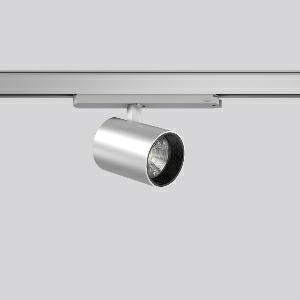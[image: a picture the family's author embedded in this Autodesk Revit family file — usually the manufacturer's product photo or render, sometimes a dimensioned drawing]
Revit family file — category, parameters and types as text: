
# Revit family: deecos_s_mini_track-in_742264_004_3_135f
name_source: partatom
category: Lighting Fixtures
units: mm (PartAtom-declared; Revit-internal decimal feet)

## family parameters
Cut with Voids When Loaded = No
Host = Face
Light Source = No
Part Type = Normal
Room Calculation Point = No
Round Connector Dimension = Use Diameter
Shared = No

## types (1)
- DEECOS S mini track-in (1 x LED Modul 935, 3300 lm, 3500)
    Apparent Load = 29 VA
    Approval mark = CE
    CIE Flux Codes = 80 99 100 100 100
    Color Rendering = 92
    Color Temperature = 3500
    Default Elevation = 1800 mm
    Description = Series: DEECOS S mini track-in
LED surface-mounted projector in modern design with no visible cooling ribs. Housing: die-cast aluminium, powder-coated. Rotation range: 356°. Swivel range: 90°. Black plastic ring and recessed LED to prevent glare from the side. Optical assembly with lens made of plastic (polycarbonate) for the best homogeneous light distribution - can be changed without tools. Best colour rendering index Ra>90. With multi adaptor for 3-circuit tracks 230 V. Suitable for Track on ceiling, Wall track. Track-in driver integrated into the adapter. High quality converter without flickering and stroboscopic effect. The following accessories can be mounted without use of tools: interchangeable lenses, decorative glasses, honeycomb louvre, clear and frosted diffusers, white interchangeable plastic ring. 
Colour: silver
Diameter: 87 mm
Height: 135 mm
Lamp: LED
Socket: without socket
Colour temperature: 3500K
Colour rendering index (CRI): 92
System power: 29 W
Rated luminous flux: 3300 lm
Luminous efficiency: 114 lm/W
Control gear: Regulated power supply
Protection class: II
Type of protection: IP 20
    Height = 135 mm
    Lamp = 1 x LED Modul 935
    Lamp Light Flux = 3300 lm
    Lamp count = 1
    Length = 87 mm
    Lifetime = 50000 h
    Luminous efficacy = 114 lm/W
    Manufacturer = RZB
    ModVariant = No
    Model = 742264.004.3
    Mounting Place = Ceiling
    Mounting Type = Rail mounted
    Number of Poles = 1
    OnlyDefault = Yes
    Power Factor = 1
    Product Name = DEECOS S mini track-in
    Product group = Track mounted projectors
    ProductGroupID = 301
    Protection Class = Protection class II
    Protection Degree = IP 20
    RLX_Detail_Level = 1
    RLX_Emergency_Light_Flux = 0 lm
    RLX_Emergency_Type = 0
    RLX_Emergency_Type_DB = No
    RlxData = <blob elided: 36353 chars, md5=88046531>
    Socket = socket
    Standby Power = 0 W
    System Light Flux = 3300 lm
    System Power = 29 W
    Type Comments = Product without accessories
    Type Image = 742108.004.jpg
    URL = http://relux.com
    VarID = ---
    Voltage = 230 V
    Voltage Range = 220-240 V
    Weight = 0.00 kg
    Width = 0 mm  [stored 0 ft]

note: [stored X ft] marks values corroborated as IEEE doubles in the binary element streams (Revit-internal decimal feet)

## geometry (parser evidence)
native form markers: Blend x4, Sweep x12
no freeform markers — native parametric forms only
